# Revit family: Скамейка стальная «Диван круглый» Арт 11354
name_source: partatom
category: Антураж
revit_build: Autodesk Revit 2018 (Build: 20180423_1000(x64)
units: mm (PartAtom-declared; Revit-internal decimal feet)

## family parameters
Всегда вертикально = Да
Источник визуального образа = Геометрия семейства
На основе рабочей плоскости = Нет
Общий = Нет
При загрузке вырезать с полостями = Нет
Точка расчета площади = Нет

## types (4) — shared parameters
URL = https://hobbyka.ru
Артикул товара = Арт. 11354
Высота = 745 мм
Группа модели = Скамейки
Изготовитель = ООО «Хоббика
Изображение типоразмера = Скамейка стальная «Диван круглый» Арт 11354 Радиусная.jpg
Материал изделия = Сталь, дерево
Цвет лавки = Дерево
Цвет опор = Сталь

## per-type parameters (varying)
| type | Версия R1000 | Версия R550 | Версия R750 | Версия «Боярд» | Длина | Описание | Ширина |
| Версия R550 | Нет | Да | Нет | Нет | 2150 мм | Скамейка стальная «Диван круглый». Версия R550 | 2150 мм |
| Версия R750 | Нет | Нет | Да | Нет | 2550 мм | Скамейка стальная «Диван круглый». Версия R750 | 2550 мм |
| Версия R1000 | Да | Нет | Нет | Нет | 3050 мм | Скамейка стальная «Диван круглый». Версия R1000 | 3050 мм |
| Версия «Боярд» | Нет | Нет | Нет | Да | 3040 мм | Скамейка стальная «Диван круглый». Версия «Боярд» | 3040 мм |
